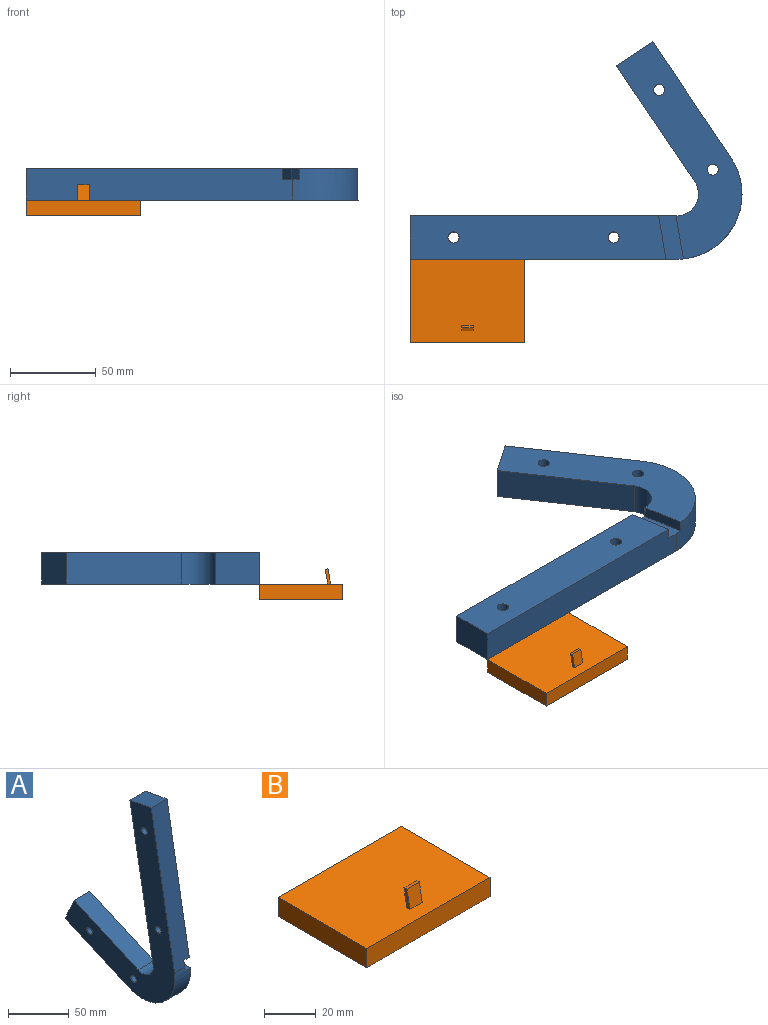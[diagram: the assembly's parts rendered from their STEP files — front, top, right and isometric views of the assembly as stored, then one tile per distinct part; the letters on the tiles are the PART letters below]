
ASSEMBLY  parts=2 mates=1
PART A: 18 faces, bbox 18.4x128.1x198 mm
  f0: plane 23.2x18.42mm, normal (0,0.91,0.41), area 467.7mm2, adj f2,f3,f5,f11
  f1: plane 153.31x27.03mm, normal (0,-0.98,0.17), area 2827.3mm2, adj f3,f4,f8,f10,f12,f13
  f2: plane 128.08x59.66mm, normal (1,0,0), area 3357.6mm2, adj f0,f5,f6,f7,f9,f11,f12,f14
  f3: plane 198.03x128.08mm, normal (-1,0,0), area 7289.6mm2, adj f0,f1,f5,f6,f7,f10,f11,f12
  f4: plane 147.22x50.97mm, normal (1,0,0), area 3674.3mm2, adj f1,f6,f8,f10,f16,f17
  f5: plane 74.49x33.16mm, normal (0,0.41,-0.91), area 1501.4mm2, adj f0,f2,f3,f12
  f6: plane 153.31x27.03mm, normal (0,0.98,-0.17), area 2802mm2, adj f2,f3,f4,f7,f8,f9,f10,f13
  f7: cylinder r=12.7mm len=18.42mm, axis (-1,0,0), area 506.1mm2, adj f2,f3,f6,f11
  f8: plane 25.79x6.38mm, normal (0,0,-1), area 164.5mm2, adj f1,f4,f6,f13
  f9: plane 25.59x6.38mm, normal (0,0,1), area 163.2mm2, adj f2,f6,f12,f13
  f10: plane 25.01x18.42mm, normal (0,0.17,0.98), area 467.7mm2, adj f1,f3,f4,f6
  f11: plane 74.49x33.16mm, normal (0,-0.41,0.91), area 1501.4mm2, adj f0,f2,f3,f7
  f12: cylinder r=38.1mm len=53.6mm, axis (-1,0,0), area 1493.3mm2, adj f1,f2,f3,f5,f9,f13
  f13: plane 27.35x10mm, normal (1,0,0), area 257.6mm2, adj f1,f6,f8,f9,f12
  f14: cylinder r=3.24mm len=18.42mm, axis (-1,0,0), area 374.7mm2, adj f2,f3
  f15: cylinder r=3.24mm len=18.42mm, axis (-1,0,0), area 374.7mm2, adj f2,f3
  f16: cylinder r=3.24mm len=18.42mm, axis (-1,0,0), area 374.7mm2, adj f3,f4
  f17: cylinder r=3.24mm len=18.42mm, axis (-1,0,0), area 374.7mm2, adj f3,f4
PART B: 11 faces, bbox 67x48.5x17.9 mm
  f0: plane 48.45x9mm, normal (1,0,0), area 436mm2, adj f1,f3,f4,f5
  f1: plane 67x9mm, normal (0,1,0), area 603mm2, adj f0,f2,f4,f5
  f2: plane 48.45x9mm, normal (-1,0,0), area 436mm2, adj f1,f3,f4,f5
  f3: plane 67x9mm, normal (0,-1,0), area 603mm2, adj f0,f2,f4,f5
  f4: plane 67x48.45mm, normal (0,0,1), area 3234.8mm2, adj f0,f1,f2,f3,f6,f8,f9,f10
  f5: plane 67x48.45mm, normal (0,0,-1), area 3246.2mm2, adj f0,f1,f2,f3
  f6: plane 8.92x3.22mm, normal (1,0,0), area 14.9mm2, adj f4,f7,f8,f9
  f7: plane 6.7x1.64mm, normal (0,0.17,0.98), area 11.2mm2, adj f6,f8,f9,f10
  f8: plane 8.63x6.7mm, normal (0,0.98,-0.17), area 58.7mm2, adj f4,f6,f7,f10
  f9: plane 8.92x6.7mm, normal (0,-0.98,0.17), area 60.7mm2, adj f4,f6,f7,f10
  f10: plane 8.92x3.22mm, normal (-1,0,0), area 14.9mm2, adj f4,f7,f8,f9
PLACE A rot(axis=(0.09,-0.99,0.09),90.4deg) t=(123.4,112.13,60.05)mm
PLACE B t=(0,75.2,5.01)mm
MATE fastened A.f3 <-> B.f4  axis (0,0,1) through (-33.5,99.43,14.01)mm
